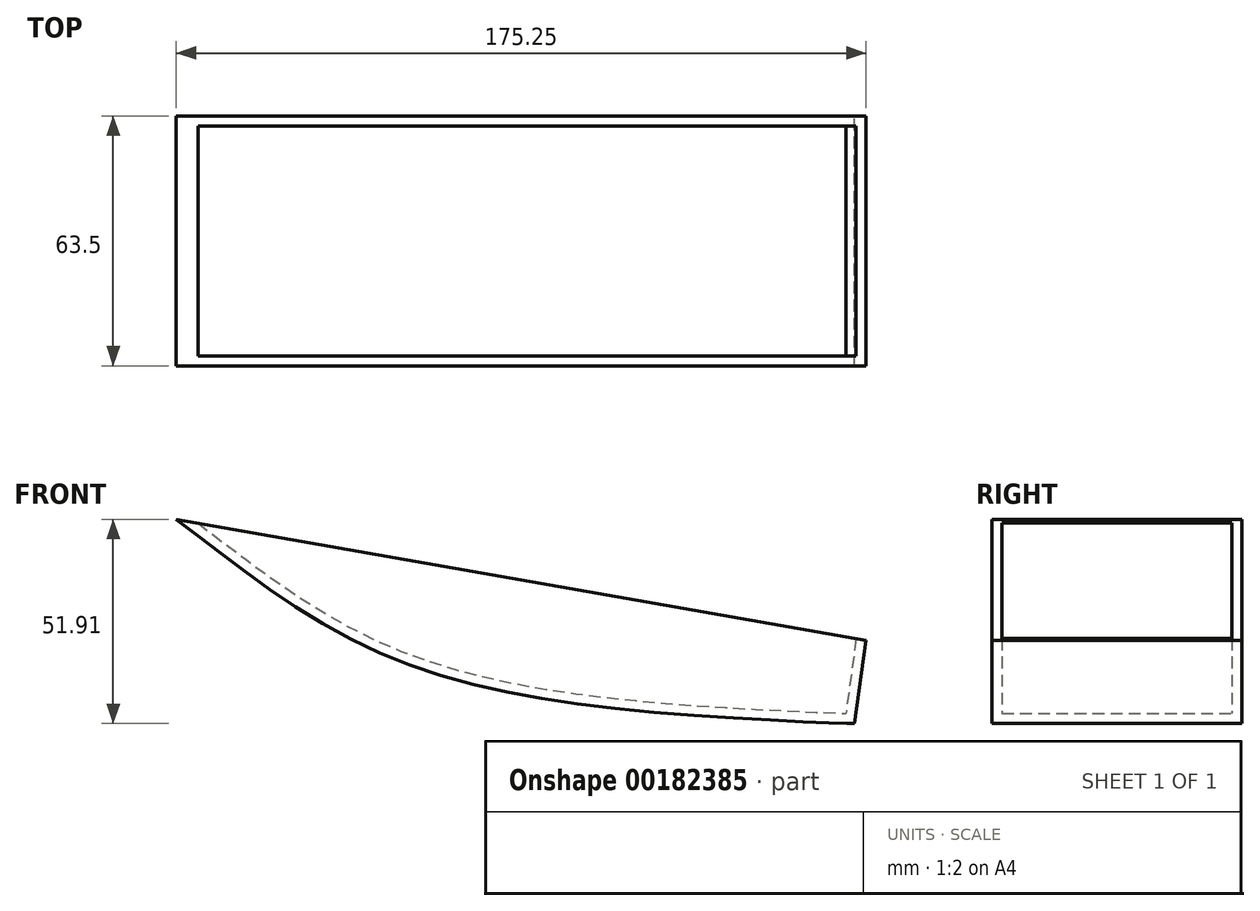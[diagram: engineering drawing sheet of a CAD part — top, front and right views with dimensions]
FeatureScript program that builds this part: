
annotation { "Feature Type Name" : "Feature", "Feature Type Description" : "" }
export const myFeature = defineFeature(function(context is Context, id is Id, definition is map)
    precondition{}
    {
        {
            var Q0;
            Q0=qCreatedBy(makeId("Front.planeOp"),FACE);
            var sketch = newSketch(context, id + "F0", { "sketchPlane" : qUnion([Q0])});
            skFitSpline(sketch, "E0", {"points": [v(-108.94, 16.34) * mm, v(-61.6, -15.64) * mm, v(11.9, -32.66) * mm, v(63.4, -35.57) * mm, v(62.98, -35.57) * mm], "startDerivative": vector(128.67, -96.13) * mm, "endDerivative": vector(-46.54, 0) * mm});
            skLineSegment(sketch, "E1", {"start": v(-108.94, 16.34) * mm, "end": v(66.3, -14.39) * mm});
            skLineSegment(sketch, "E2", {"start": v(66.3, -14.39) * mm, "end": v(63.4, -35.57) * mm});
            skSolve(sketch);
        }
        {
            var Q0;
            Q0 = qSketchRegion(id + "F0", true);
            extrude(context, id + "F1", {"entities" : qUnion([Q0]), "depth" : 63.5 * mm});
        }
        {
            var Q0;
            Q0=makeQuery(id+"F1.opExtrude","SWEPT_FACE",FACE,{"disambiguationData":[OSD([sQuery(id+"F0.wireOp",EDGE,"E1")])]});
            shell(context, id + "F2", {"entities" : qUnion([Q0]), "thickness" : 2.54 * mm});
        }
    });
